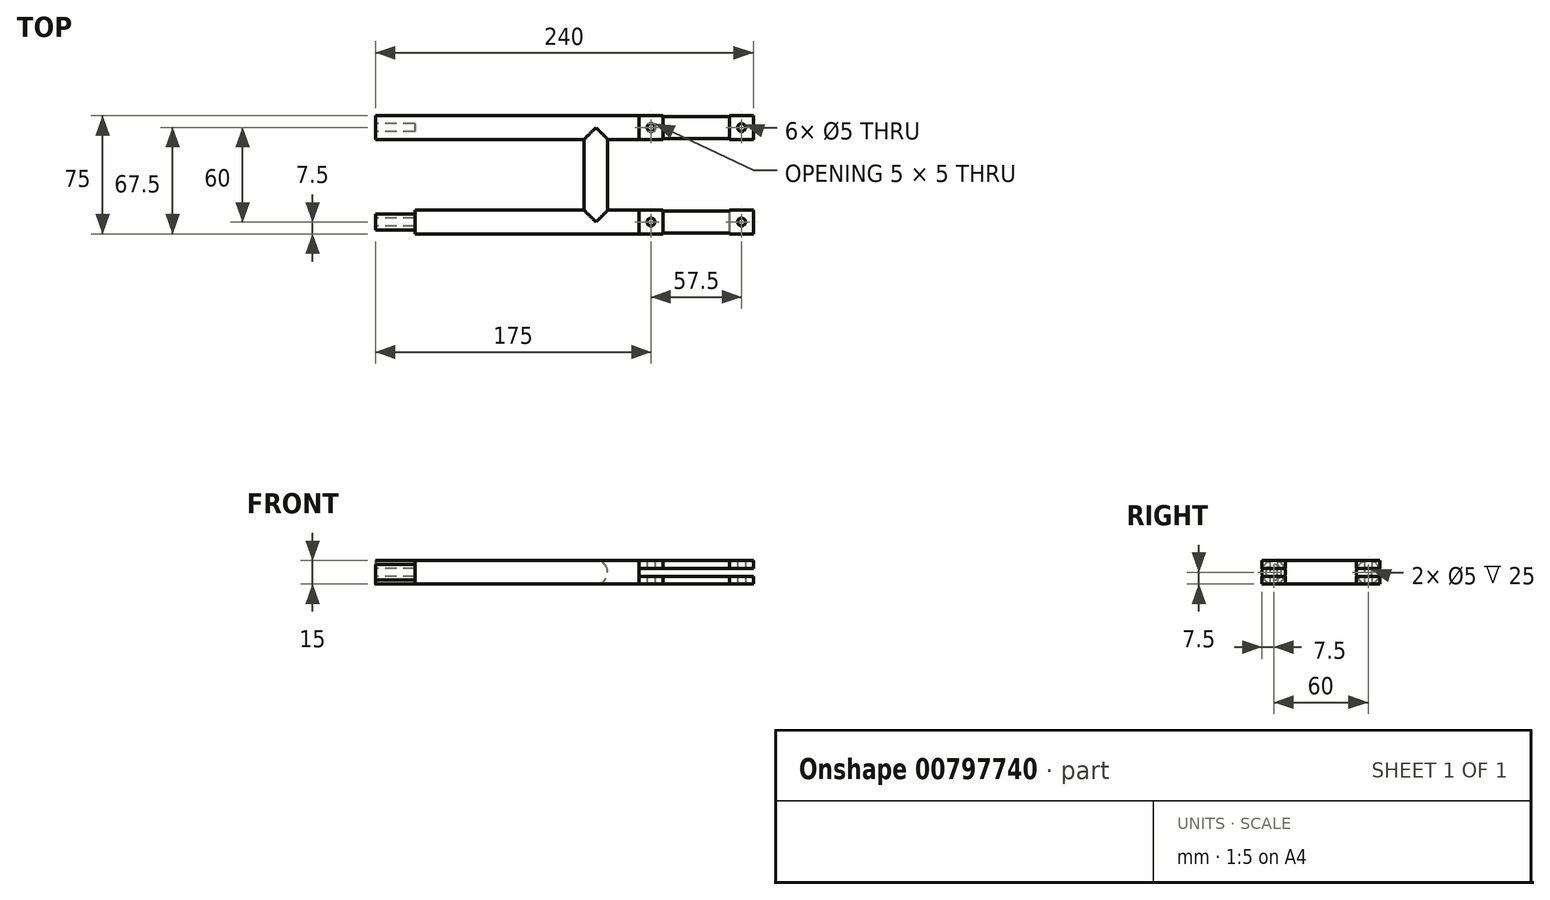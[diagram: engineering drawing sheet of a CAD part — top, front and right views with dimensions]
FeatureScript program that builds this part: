
annotation { "Feature Type Name" : "Feature", "Feature Type Description" : "" }
export const myFeature = defineFeature(function(context is Context, id is Id, definition is map)
    precondition{}
    {
        {
            var Q0;
            Q0=qCreatedBy(makeId("Top.planeOp"),FACE);
            var sketch = newSketch(context, id + "F0", { "sketchPlane" : qUnion([Q0])});
            skLineSegment(sketch, "E0", {"start": v(0, -30) * mm, "end": v(0, 30) * mm, "construction": true});
            skLineSegment(sketch, "E1", {"start": v(0, -30) * mm, "end": v(-240, -30) * mm, "construction": true});
            skLineSegment(sketch, "E2", {"start": v(-240, -30) * mm, "end": v(-240, 30) * mm, "construction": true});
            skLineSegment(sketch, "E3", {"start": v(-240, 30) * mm, "end": v(0, 30) * mm, "construction": true});
            skLineSegment(sketch, "E4.bottom", {"start": v(-240, -37.5) * mm, "end": v(0, -37.5) * mm});
            skLineSegment(sketch, "E4.top", {"start": v(-240, -22.5) * mm, "end": v(-115, -22.5) * mm});
            skLineSegment(sketch, "E4.left", {"start": v(-240, -37.5) * mm, "end": v(-240, -22.5) * mm});
            skPoint(sketch, "E4.middle", {"position": v(0, -30) * mm});
            skLineSegment(sketch, "E5", {"start": v(0, -37.5) * mm, "end": v(0, -22.5) * mm});
            skLineSegment(sketch, "E6.MirrorCS", {"start": v(-240, 37.5) * mm, "end": v(0, 37.5) * mm});
            skLineSegment(sketch, "E7.MirrorCS", {"start": v(0, 37.5) * mm, "end": v(0, 22.5) * mm});
            skLineSegment(sketch, "E8.MirrorCS", {"start": v(-240, 22.5) * mm, "end": v(-115, 22.5) * mm});
            skLineSegment(sketch, "E9.MirrorCS", {"start": v(-240, 37.5) * mm, "end": v(-240, 22.5) * mm});
            skPoint(sketch, "E10", {"position": v(-50, -30) * mm});
            skPoint(sketch, "E11", {"position": v(-50, 30) * mm});
            skLineSegment(sketch, "E12.left", {"start": v(-100, -22.5) * mm, "end": v(-100, 22.5) * mm});
            skLineSegment(sketch, "E12.right", {"start": v(-115, -22.5) * mm, "end": v(-115, 22.5) * mm});
            skLineSegment(sketch, "E13.trimOffspring", {"start": v(-100, -22.5) * mm, "end": v(0, -22.5) * mm});
            skLineSegment(sketch, "E14.trimOffspring", {"start": v(-100, 22.5) * mm, "end": v(0, 22.5) * mm});
            skPoint(sketch, "E15", {"position": v(-100, -30) * mm});
            skPoint(sketch, "E16", {"position": v(-100, 30) * mm});
            skLineSegment(sketch, "E17", {"start": v(-100, -30) * mm, "end": v(-100, 30) * mm, "construction": true});
            skPoint(sketch, "E18", {"position": v(-100, 0) * mm});
            skSolve(sketch);
        }
        {
            var Q0;
            Q0=makeQuery(id+"F0.imprint","IMPRINT",FACE,{"disambiguationData":[TD([[makeQuery(id+"F0.imprint","IMPRINT",EDGE,{"derivedFrom":sQuery(id+"F0.wireOp",EDGE,"E4.bottom")}),1.0]])]});
            extrude(context, id + "F1", {"entities" : qUnion([Q0]), "depth" : 15 * mm, "offsetDistance" : 25 * mm});
        }
        {
            var Q0;
            Q0=qCreatedBy(makeId("Right.planeOp"),FACE);
            var sketch = newSketch(context, id + "F2", { "sketchPlane" : qUnion([Q0])});
            skLineSegment(sketch, "E19", {"start": v(0, 0) * mm, "end": v(0, 7.5) * mm, "construction": true});
            skLineSegment(sketch, "E20", {"start": v(-37.5, 7.5) * mm, "end": v(37.5, 7.5) * mm, "construction": true});
            skPoint(sketch, "E21", {"position": v(-30, 7.5) * mm});
            skPoint(sketch, "E22", {"position": v(30, 7.5) * mm});
            skCircle(sketch, "E23", {"center": v(-30, 7.5) * mm, "radius": 7.5 * mm});
            skCircle(sketch, "E24", {"center": v(30, 7.5) * mm, "radius": 7.5 * mm});
            skSolve(sketch);
        }
        {
            var Q0;
            Q0=qSketchRegion(id+"F2",true);
            extrude(context, id + "F3", {"entities" : qUnion([Q0]), "operationType" : NewBodyOperationType.INTERSECT, "oppositeDirection" : true, "depth" : 240 * mm, "offsetDistance" : 25 * mm});
        }
        {
            var Q0;
            Q0=qCreatedBy(makeId("Front.planeOp"),FACE);
            var sketch = newSketch(context, id + "F4", { "sketchPlane" : qUnion([Q0])});
            skLineSegment(sketch, "E25", {"start": v(0, 0) * mm, "end": v(0, 7.5) * mm, "construction": true});
            skLineSegment(sketch, "E26", {"start": v(0, 7.5) * mm, "end": v(-100, 7.5) * mm, "construction": true});
            skCircle(sketch, "E27", {"center": v(-100, 7.5) * mm, "radius": 7.5 * mm});
            skSolve(sketch);
        }
        {
            var Q0;
            Q0=qSketchRegion(id+"F4",true);
            extrude(context, id + "F5", {"entities" : qUnion([Q0]), "operationType" : NewBodyOperationType.ADD, "depth" : 30 * mm, "offsetDistance" : 25 * mm, "hasSecondDirection" : true, "secondDirectionOppositeDirection" : true, "secondDirectionDepth" : 30 * mm});
        }
        {
            var Q0;
            Q0=qCreatedBy(makeId("Top.planeOp"),FACE);
            var sketch = newSketch(context, id + "F6", { "sketchPlane" : qUnion([Q0])});
            skLineSegment(sketch, "E28", {"start": v(0, 0) * mm, "end": v(0, 37.5) * mm, "construction": true});
            skLineSegment(sketch, "E29", {"start": v(0, 37.5) * mm, "end": v(-72.5, 37.5) * mm, "construction": true});
            skLineSegment(sketch, "E30", {"start": v(-72.5, 37.5) * mm, "end": v(-72.5, -37.5) * mm, "construction": true});
            skLineSegment(sketch, "E31", {"start": v(-72.5, -37.5) * mm, "end": v(0, -37.5) * mm, "construction": true});
            skLineSegment(sketch, "E32", {"start": v(0, -37.5) * mm, "end": v(0, 0) * mm, "construction": true});
            skPoint(sketch, "E33", {"position": v(-72.5, 22.5) * mm});
            skPoint(sketch, "E34", {"position": v(-72.5, -22.5) * mm});
            skPoint(sketch, "E35", {"position": v(0, -22.5) * mm});
            skPoint(sketch, "E36", {"position": v(0, 22.5) * mm});
            skPoint(sketch, "E37", {"position": v(-57.5, 37.5) * mm});
            skPoint(sketch, "E38", {"position": v(-57.5, -37.5) * mm});
            skPoint(sketch, "E39", {"position": v(-15, 37.5) * mm});
            skPoint(sketch, "E40", {"position": v(-15, -37.5) * mm});
            skLineSegment(sketch, "E41", {"start": v(-72.5, 37.5) * mm, "end": v(-57.5, 37.5) * mm});
            skLineSegment(sketch, "E42", {"start": v(-57.5, 22.5) * mm, "end": v(-72.5, 22.5) * mm});
            skLineSegment(sketch, "E43", {"start": v(-57.5, 22.5) * mm, "end": v(-57.5, 37.5) * mm});
            skLineSegment(sketch, "E44", {"start": v(-72.5, -22.5) * mm, "end": v(-57.5, -22.5) * mm});
            skLineSegment(sketch, "E45", {"start": v(-57.5, -37.5) * mm, "end": v(-57.5, -22.5) * mm});
            skLineSegment(sketch, "E46", {"start": v(-57.5, -37.5) * mm, "end": v(-72.5, -37.5) * mm});
            skLineSegment(sketch, "E47", {"start": v(-72.5, -37.5) * mm, "end": v(-72.5, -22.5) * mm});
            skLineSegment(sketch, "E48", {"start": v(-72.5, 22.5) * mm, "end": v(-72.5, 37.5) * mm});
            skLineSegment(sketch, "E49", {"start": v(0, 37.5) * mm, "end": v(-15, 37.5) * mm});
            skLineSegment(sketch, "E50", {"start": v(-15, 37.5) * mm, "end": v(-15, 22.5) * mm});
            skLineSegment(sketch, "E51", {"start": v(0, 22.5) * mm, "end": v(-15, 22.5) * mm});
            skLineSegment(sketch, "E52", {"start": v(0, 22.5) * mm, "end": v(0, 37.5) * mm});
            skLineSegment(sketch, "E53", {"start": v(0, -22.5) * mm, "end": v(0, -37.5) * mm});
            skLineSegment(sketch, "E54", {"start": v(0, -37.5) * mm, "end": v(-15, -37.5) * mm});
            skLineSegment(sketch, "E55", {"start": v(-15, -37.5) * mm, "end": v(-15, -22.5) * mm});
            skLineSegment(sketch, "E56", {"start": v(0, -22.5) * mm, "end": v(-15, -22.5) * mm});
            skSolve(sketch);
        }
        {
            var Q0;
            Q0=qSketchRegion(id+"F6",true);
            extrude(context, id + "F7", {"entities" : qUnion([Q0]), "operationType" : NewBodyOperationType.ADD, "depth" : 15 * mm, "offsetDistance" : 25 * mm});
        }
        {
            var Q0;
            Q0=qCreatedBy(makeId("Front.planeOp"),FACE);
            var sketch = newSketch(context, id + "F8", { "sketchPlane" : qUnion([Q0])});
            skLineSegment(sketch, "E57", {"start": v(0, 0) * mm, "end": v(0, 10) * mm, "construction": true});
            skLineSegment(sketch, "E58", {"start": v(0, 10) * mm, "end": v(-72.5, 10) * mm, "construction": true});
            skLineSegment(sketch, "E59", {"start": v(-72.5, 10) * mm, "end": v(-72.5, 5) * mm, "construction": true});
            skLineSegment(sketch, "E60", {"start": v(-72.5, 5) * mm, "end": v(-57.5, 5) * mm, "construction": true});
            skLineSegment(sketch, "E61", {"start": v(-57.5, 5) * mm, "end": v(-57.5, 0) * mm, "construction": true});
            skLineSegment(sketch, "E62", {"start": v(-57.5, 0) * mm, "end": v(0, 0) * mm, "construction": true});
            skLineSegment(sketch, "E63", {"start": v(-72.5, 5) * mm, "end": v(-72.5, -2.5) * mm, "construction": true});
            skLineSegment(sketch, "E64", {"start": v(0, 10) * mm, "end": v(0, 0) * mm});
            skLineSegment(sketch, "E65", {"start": v(0, 0) * mm, "end": v(0, 7.5) * mm, "construction": true});
            skLineSegment(sketch, "E66", {"start": v(0, 7.5) * mm, "end": v(-7.5, 7.5) * mm, "construction": true});
            skLineSegment(sketch, "E67", {"start": v(-57.5, 0) * mm, "end": v(0, 0) * mm});
            skLineSegment(sketch, "E68", {"start": v(-72.5, 10) * mm, "end": v(0, 10) * mm});
            skLineSegment(sketch, "E69", {"start": v(-72.5, 5) * mm, "end": v(-57.5, 5) * mm});
            skLineSegment(sketch, "E70", {"start": v(-57.5, 5) * mm, "end": v(-57.5, 0) * mm});
            skLineSegment(sketch, "E71", {"start": v(-72.5, 10) * mm, "end": v(-72.5, 5) * mm});
            skSolve(sketch);
        }
        {
            var Q0;
            Q0=qSketchRegion(id+"F8",true);
            extrude(context, id + "F9", {"entities" : qUnion([Q0]), "operationType" : NewBodyOperationType.REMOVE, "oppositeDirection" : true, "depth" : 40.1 * mm, "offsetDistance" : 25 * mm});
        }
        {
            var Q0;
            Q0=qCreatedBy(makeId("Front.planeOp"),FACE);
            var sketch = newSketch(context, id + "F10", { "sketchPlane" : qUnion([Q0])});
            skLineSegment(sketch, "E72", {"start": v(0, 0) * mm, "end": v(0, 5) * mm, "construction": true});
            skLineSegment(sketch, "E73", {"start": v(0, 5) * mm, "end": v(0, 10) * mm, "construction": true});
            skLineSegment(sketch, "E74", {"start": v(0, 10) * mm, "end": v(0, 15) * mm, "construction": true});
            skLineSegment(sketch, "E75", {"start": v(0, 15) * mm, "end": v(-57.5, 15) * mm});
            skLineSegment(sketch, "E76", {"start": v(-57.5, 15) * mm, "end": v(-57.5, 10) * mm});
            skLineSegment(sketch, "E77", {"start": v(-57.5, 10) * mm, "end": v(-72.5, 10) * mm});
            skLineSegment(sketch, "E78", {"start": v(-72.5, 10) * mm, "end": v(-72.5, 5) * mm});
            skLineSegment(sketch, "E79", {"start": v(-72.5, 5) * mm, "end": v(-57.5, 5) * mm});
            skLineSegment(sketch, "E80", {"start": v(-57.5, 5) * mm, "end": v(0, 5) * mm});
            skLineSegment(sketch, "E81", {"start": v(0, 5) * mm, "end": v(0, 15) * mm});
            skSolve(sketch);
        }
        {
            var Q0;
            Q0=makeQuery(id+"F10.imprint","IMPRINT",FACE,{"disambiguationData":[TD([[makeQuery(id+"F10.imprint","IMPRINT",EDGE,{"derivedFrom":sQuery(id+"F10.wireOp",EDGE,"E75")}),1.0]])]});
            extrude(context, id + "F11", {"entities" : qUnion([Q0]), "operationType" : NewBodyOperationType.REMOVE, "depth" : 54.1 * mm, "offsetDistance" : 25 * mm});
        }
        {
            var Q0;
            Q0=qCreatedBy(makeId("Top.planeOp"),FACE);
            var sketch = newSketch(context, id + "F12", { "sketchPlane" : qUnion([Q0])});
            skLineSegment(sketch, "E82", {"start": v(0, -37.5) * mm, "end": v(0, 37.5) * mm, "construction": true});
            skPoint(sketch, "E83", {"position": v(0, -30) * mm});
            skPoint(sketch, "E84", {"position": v(0, 30) * mm});
            skLineSegment(sketch, "E85", {"start": v(0, -30) * mm, "end": v(-65, -30) * mm, "construction": true});
            skLineSegment(sketch, "E86", {"start": v(0, 30) * mm, "end": v(-65, 30) * mm, "construction": true});
            skPoint(sketch, "E87", {"position": v(-7.5, 30) * mm});
            skPoint(sketch, "E88", {"position": v(-7.5, -30) * mm});
            skCircle(sketch, "E89", {"center": v(-65, 30) * mm, "radius": 2.5 * mm});
            skCircle(sketch, "E90", {"center": v(-65, -30) * mm, "radius": 2.5 * mm});
            skCircle(sketch, "E91", {"center": v(-7.5, -30) * mm, "radius": 2.5 * mm});
            skCircle(sketch, "E92", {"center": v(-7.5, 30) * mm, "radius": 2.5 * mm});
            skSolve(sketch);
        }
        {
            var Q0;
            Q0=qSketchRegion(id+"F12",true);
            extrude(context, id + "F13", {"entities" : qUnion([Q0]), "operationType" : NewBodyOperationType.REMOVE, "depth" : 25 * mm, "offsetDistance" : 25 * mm});
        }
        {
            var Q0;
            Q0=makeQuery(id+"F1.opExtrude","SWEPT_FACE",FACE,{"disambiguationData":[OSD([sQuery(id+"F0.wireOp",EDGE,"E4.left")])]});
            cPlane(context, id + "F14", {"entities" : qUnion([Q0]), "cplaneType" : CPlaneType.OFFSET, "offset" : 0 * mm, "width" : 150 * mm, "height" : 150 * mm});
        }
        {
            var Q0;
            Q0=qCreatedBy(id+"F14.planeOp",FACE);
            var sketch = newSketch(context, id + "F15", { "sketchPlane" : qUnion([Q0])});
            skLineSegment(sketch, "E93", {"start": v(0, 0) * mm, "end": v(0, 7.5) * mm, "construction": true});
            skLineSegment(sketch, "E94", {"start": v(-30, 7.5) * mm, "end": v(30, 7.5) * mm, "construction": true});
            skCircle(sketch, "E95", {"center": v(30, 7.5) * mm, "radius": 2.5 * mm});
            skCircle(sketch, "E96", {"center": v(-30, 7.5) * mm, "radius": 2.5 * mm});
            skSolve(sketch);
        }
        {
            var Q0;
            Q0=qSketchRegion(id+"F15",true);
            extrude(context, id + "F16", {"entities" : qUnion([Q0]), "operationType" : NewBodyOperationType.REMOVE, "oppositeDirection" : true, "depth" : 25 * mm, "offsetDistance" : 25 * mm});
        }
        {
            var Q0;
            Q0=qCreatedBy(id+"F14.planeOp",FACE);
            var sketch = newSketch(context, id + "F17", { "sketchPlane" : qUnion([Q0])});
            skLineSegment(sketch, "E97", {"start": v(0, 0) * mm, "end": v(0, 7.5) * mm, "construction": true});
            skLineSegment(sketch, "E98", {"start": v(30, 7.5) * mm, "end": v(-30, 7.5) * mm, "construction": true});
            skCircle(sketch, "E99", {"center": v(30, 7.5) * mm, "radius": 5 * mm});
            skCircle(sketch, "E100", {"center": v(30, 7.5) * mm, "radius": 7.5 * mm});
            skCircle(sketch, "E101.MirrorC", {"center": v(-30, 7.5) * mm, "radius": 7.5 * mm});
            skCircle(sketch, "E102.MirrorC", {"center": v(-30, 7.5) * mm, "radius": 5 * mm});
            skSolve(sketch);
        }
        {
            var Q0;
            Q0=makeQuery(id+"F17.imprint","IMPRINT",FACE,{"disambiguationData":[TD([[makeQuery(id+"F17.imprint","IMPRINT",EDGE,{"derivedFrom":sQuery(id+"F17.wireOp",EDGE,"E99")}),-1.0]])]});
            var Q1;
            Q1=makeQuery(id+"F17.imprint","IMPRINT",FACE,{"disambiguationData":[TD([[makeQuery(id+"F17.imprint","IMPRINT",EDGE,{"derivedFrom":sQuery(id+"F17.wireOp",EDGE,"E101.MirrorC")}),-1.0]])]});
            extrude(context, id + "F18", {"entities" : qUnion([Q0, Q1]), "operationType" : NewBodyOperationType.REMOVE, "oppositeDirection" : true, "depth" : 25 * mm, "offsetDistance" : 25 * mm});
        }
    });
